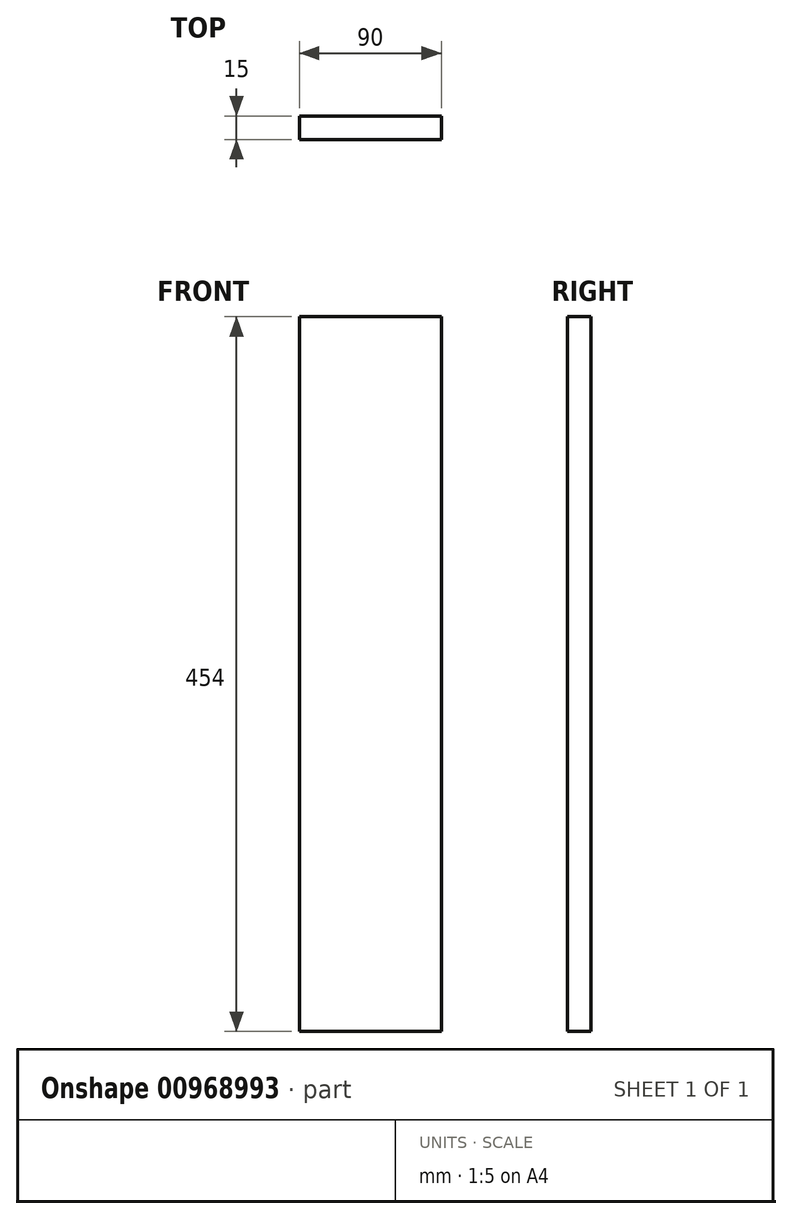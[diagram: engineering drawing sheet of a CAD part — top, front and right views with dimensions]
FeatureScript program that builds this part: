
annotation { "Feature Type Name" : "Feature", "Feature Type Description" : "" }
export const myFeature = defineFeature(function(context is Context, id is Id, definition is map)
    precondition{}
    {
        {
            var Q0;
            Q0=qCreatedBy(makeId("Front.planeOp"),FACE);
            var sketch = newSketch(context, id + "F0", { "sketchPlane" : qUnion([Q0])});
            skLineSegment(sketch, "E0.bottom", {"start": v(45, 227) * mm, "end": v(-45, 227) * mm});
            skLineSegment(sketch, "E0.top", {"start": v(45, -227) * mm, "end": v(-45, -227) * mm});
            skLineSegment(sketch, "E0.left", {"start": v(45, 227) * mm, "end": v(45, -227) * mm});
            skLineSegment(sketch, "E0.right", {"start": v(-45, 227) * mm, "end": v(-45, -227) * mm});
            skPoint(sketch, "E0.middle", {"position": v(0, 0) * mm});
            skSolve(sketch);
        }
        {
            var Q0;
            Q0=makeQuery(id+"F0.imprint","IMPRINT",FACE,{"disambiguationData":[TD([[makeQuery(id+"F0.imprint","IMPRINT",EDGE,{"derivedFrom":sQuery(id+"F0.wireOp",EDGE,"E0.bottom")}),1.0]])]});
            extrude(context, id + "F1", {"entities" : qUnion([Q0]), "depth" : 15 * mm, "offsetDistance" : 25 * mm});
        }
    });
